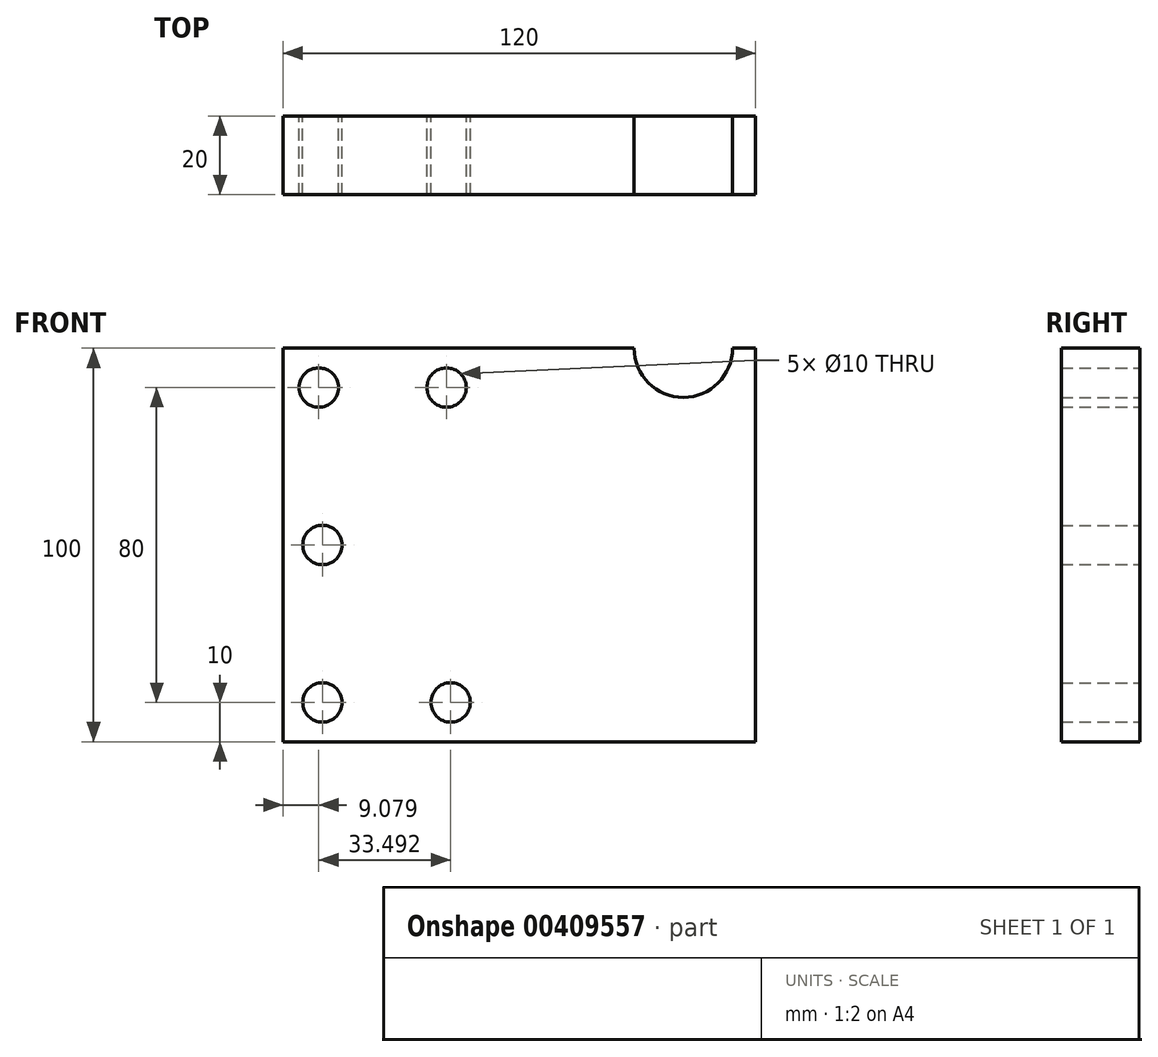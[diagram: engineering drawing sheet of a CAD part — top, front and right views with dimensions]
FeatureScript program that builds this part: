
annotation { "Feature Type Name" : "Feature", "Feature Type Description" : "" }
export const myFeature = defineFeature(function(context is Context, id is Id, definition is map)
    precondition{}
    {
        {
            var Q0;
            Q0=qCreatedBy(makeId("Front.planeOp"),FACE);
            var sketch = newSketch(context, id + "F0", { "sketchPlane" : qUnion([Q0])});
            skLineSegment(sketch, "E0.bottom", {"start": v(-60, 50) * mm, "end": v(29.2, 50) * mm});
            skLineSegment(sketch, "E0.top", {"start": v(-60, -50) * mm, "end": v(60, -50) * mm});
            skLineSegment(sketch, "E0.left", {"start": v(-60, 50) * mm, "end": v(-60, -50) * mm});
            skLineSegment(sketch, "E0.right", {"start": v(60, 50) * mm, "end": v(60, -50) * mm});
            skPoint(sketch, "E0.middle", {"position": v(0, 0) * mm});
            skCircle(sketch, "E1", {"center": v(-50.92, 40) * mm, "radius": 5 * mm});
            skCircle(sketch, "E2", {"center": v(-50, -40) * mm, "radius": 5 * mm});
            skCircle(sketch, "E3", {"center": v(-50, 0) * mm, "radius": 5 * mm});
            skCircle(sketch, "E4", {"center": v(-18.45, 40) * mm, "radius": 5 * mm});
            skCircle(sketch, "E5", {"center": v(-17.43, -40) * mm, "radius": 5 * mm});
            skArc(sketch, "E6", {"start": v(29.2, 50) * mm, "mid": v(41.7, 37.5) * mm, "end": v(54.2, 50) * mm});
            skLineSegment(sketch, "E7.trimOffspring", {"start": v(54.2, 50) * mm, "end": v(60, 50) * mm});
            skSolve(sketch);
        }
        {
            var Q0;
            Q0=makeQuery(id+"F0.imprint","IMPRINT",FACE,{"disambiguationData":[TD([[makeQuery(id+"F0.imprint","IMPRINT",EDGE,{"derivedFrom":sQuery(id+"F0.wireOp",EDGE,"E0.bottom")}),-1.0]])]});
            var sketch = newSketch(context, id + "F1", { "sketchPlane" : qUnion([Q0])});
            skSolve(sketch);
        }
        {
            var Q0;
            Q0 = qSketchRegion(id + "F1", true);
            var Q1;
            Q1=makeQuery(id+"F0.imprint","IMPRINT",FACE,{"disambiguationData":[TD([[makeQuery(id+"F0.imprint","IMPRINT",EDGE,{"derivedFrom":sQuery(id+"F0.wireOp",EDGE,"E0.bottom")}),-1.0]])]});
            extrude(context, id + "F2", {"entities" : qUnion([Q0, Q1]), "depth" : 20 * mm});
        }
    });
